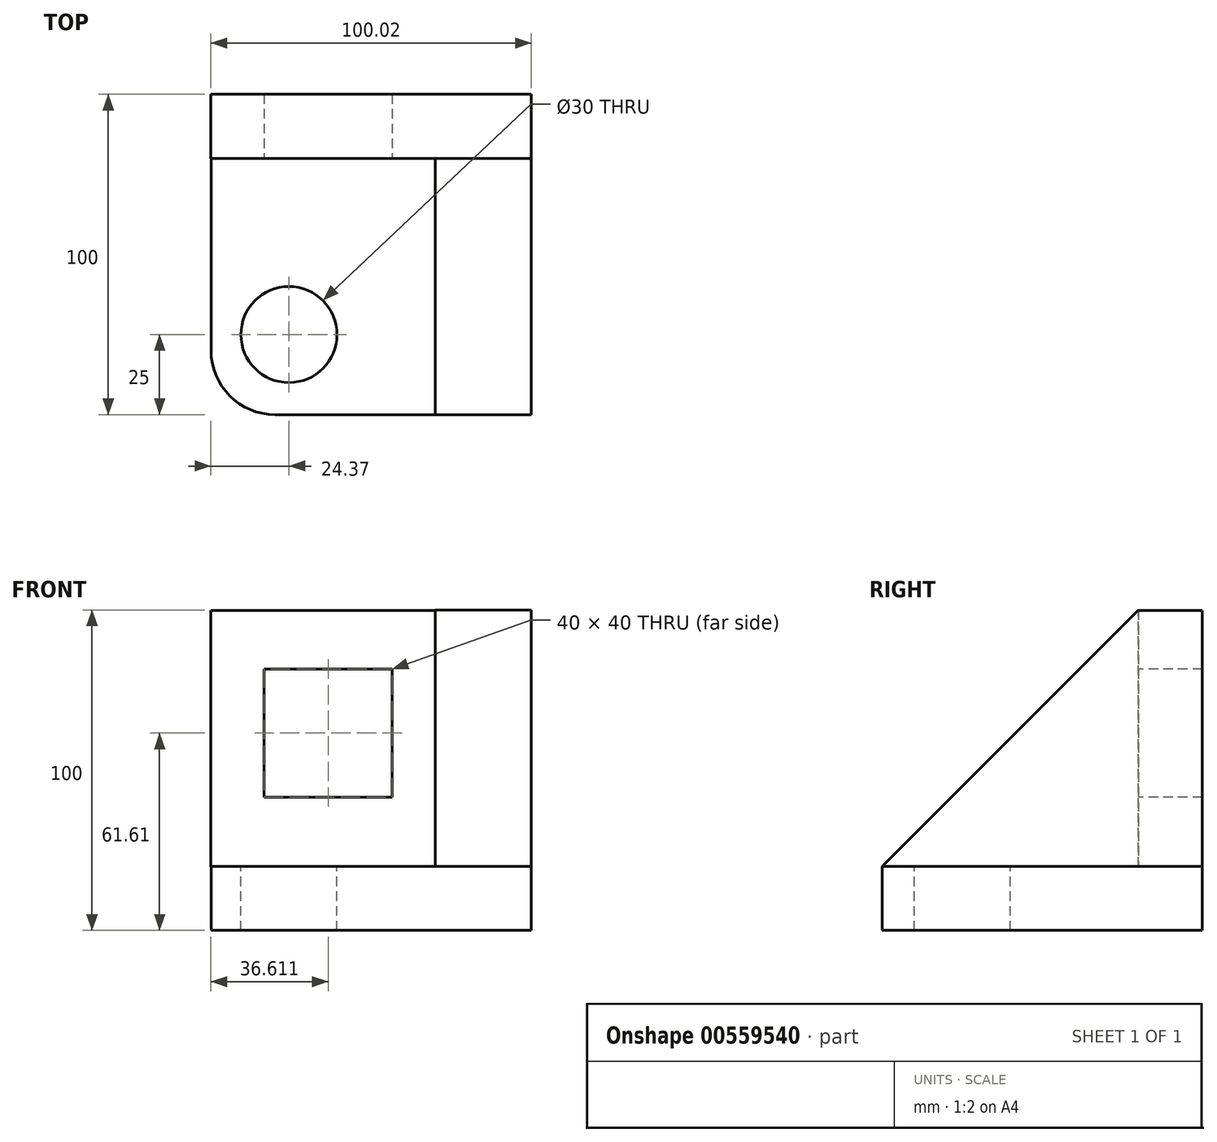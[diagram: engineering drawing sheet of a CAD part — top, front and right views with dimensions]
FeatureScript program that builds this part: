
annotation { "Feature Type Name" : "Feature", "Feature Type Description" : "" }
export const myFeature = defineFeature(function(context is Context, id is Id, definition is map)
    precondition{}
    {
        {
            var Q0;
            Q0=qCreatedBy(makeId("Top.planeOp"),FACE);
            var sketch = newSketch(context, id + "F0", { "sketchPlane" : qUnion([Q0])});
            skPoint(sketch, "E0.middle", {"position": v(0, 0) * mm});
            skLineSegment(sketch, "E1.bottom", {"start": v(-49.83, 0) * mm, "end": v(50.17, 0) * mm});
            skLineSegment(sketch, "E1.top", {"start": v(-49.83, -100) * mm, "end": v(50.17, -100) * mm});
            skLineSegment(sketch, "E1.left", {"start": v(-49.83, 0) * mm, "end": v(-49.83, -100) * mm});
            skLineSegment(sketch, "E1.right", {"start": v(50.17, 0) * mm, "end": v(50.17, -100) * mm});
            skSolve(sketch);
        }
        {
            var Q0;
            Q0 = qSketchRegion(id + "F0", true);
            extrude(context, id + "F1", {"entities" : qUnion([Q0]), "depth" : 20 * mm, "offsetDistance" : 25 * mm});
        }
        {
            var Q0;
            Q0=qCreatedBy(makeId("Front.planeOp"),FACE);
            var sketch = newSketch(context, id + "F2", { "sketchPlane" : qUnion([Q0])});
            skLineSegment(sketch, "E2.bottom", {"start": v(-49.85, 19.88) * mm, "end": v(50.15, 19.88) * mm});
            skLineSegment(sketch, "E2.top", {"start": v(-49.85, 99.88) * mm, "end": v(50.15, 99.88) * mm});
            skLineSegment(sketch, "E2.left", {"start": v(-49.85, 19.88) * mm, "end": v(-49.85, 99.88) * mm});
            skLineSegment(sketch, "E2.right", {"start": v(50.15, 19.88) * mm, "end": v(50.15, 99.88) * mm});
            skSolve(sketch);
        }
        {
            var Q0;
            Q0 = qSketchRegion(id + "F2", true);
            extrude(context, id + "F3", {"entities" : qUnion([Q0]), "operationType" : NewBodyOperationType.ADD, "depth" : 20 * mm, "offsetDistance" : 25 * mm});
        }
        {
            var Q0;
            Q0=makeQuery(id+"F1.opExtrude","CAP_FACE",FACE,{"disambiguationData":[OSD([sQuery(id+"F0.wireOp",EDGE,"E1.bottom"),sQuery(id+"F0.wireOp",EDGE,"E1.top"),sQuery(id+"F0.wireOp",EDGE,"E1.left"),sQuery(id+"F0.wireOp",EDGE,"E1.right")])],"isStart":false});
            var sketch = newSketch(context, id + "F4", { "sketchPlane" : qUnion([Q0])});
            skLineSegment(sketch, "E3.bottom", {"start": v(50.15, -20) * mm, "end": v(20.15, -20) * mm});
            skLineSegment(sketch, "E3.top", {"start": v(50.15, -100) * mm, "end": v(20.15, -100) * mm});
            skLineSegment(sketch, "E3.left", {"start": v(50.15, -20) * mm, "end": v(50.15, -100) * mm});
            skLineSegment(sketch, "E3.right", {"start": v(20.15, -20) * mm, "end": v(20.15, -100) * mm});
            skSolve(sketch);
        }
        {
            var Q0;
            Q0 = qSketchRegion(id + "F4", true);
            extrude(context, id + "F5", {"entities" : qUnion([Q0]), "operationType" : NewBodyOperationType.ADD, "depth" : 80 * mm, "offsetDistance" : 25 * mm});
        }
        {
            var Q0;
            Q0=makeQuery(id+"F1.opExtrude","SWEPT_EDGE",EDGE,{"disambiguationData":[OSD([sQuery(id+"F0.wireOp",EDGE,"E1.top"),sQuery(id+"F0.wireOp",EDGE,"E1.left")])]});
            fillet(context, id + "F6", {"entities" : qUnion([Q0]), "radius" : 20 * mm, "tangentPropagation" : true, "allowEdgeOverflow" : false});
        }
        {
            var Q0;
            {var subQ0=sQuery(id+"F0.wireOp",EDGE,"E1.top");var subQ1=sQuery(id+"F0.wireOp",EDGE,"E1.left");Q0=makeQuery(id+"F5.boolean.opBoolean","SPLIT",FACE,{"disambiguationData":[TD([makeQuery(id+"F1.opExtrude","SWEPT_FACE",FACE,{"disambiguationData":[OSD([subQ1])]})])],"derivedFrom":makeQuery(id+"F1.opExtrude","CAP_FACE",FACE,{"disambiguationData":[OSD([sQuery(id+"F0.wireOp",EDGE,"E1.bottom"),subQ0,subQ1,sQuery(id+"F0.wireOp",EDGE,"E1.right")])],"isStart":false})});}
            var sketch = newSketch(context, id + "F7", { "sketchPlane" : qUnion([Q0])});
            skCircle(sketch, "E4", {"center": v(-25.48, -75) * mm, "radius": 15 * mm});
            skSolve(sketch);
        }
        {
            var Q0;
            Q0 = qSketchRegion(id + "F7", true);
            extrude(context, id + "F8", {"entities" : qUnion([Q0]), "operationType" : NewBodyOperationType.REMOVE, "oppositeDirection" : true, "depth" : 20 * mm, "offsetDistance" : 25 * mm});
        }
        {
            var Q0;
            Q0=makeQuery(id+"F3.opExtrude","CAP_FACE",FACE,{"disambiguationData":[OSD([sQuery(id+"F2.wireOp",EDGE,"E2.bottom"),sQuery(id+"F2.wireOp",EDGE,"E2.top"),sQuery(id+"F2.wireOp",EDGE,"E2.left"),sQuery(id+"F2.wireOp",EDGE,"E2.right")])],"isStart":false});
            var sketch = newSketch(context, id + "F9", { "sketchPlane" : qUnion([Q0])});
            skLineSegment(sketch, "E5.bottom", {"start": v(6.76, 81.6) * mm, "end": v(-33.24, 81.6) * mm});
            skLineSegment(sketch, "E5.top", {"start": v(6.76, 41.6) * mm, "end": v(-33.24, 41.6) * mm});
            skLineSegment(sketch, "E5.left", {"start": v(6.76, 81.6) * mm, "end": v(6.76, 41.6) * mm});
            skLineSegment(sketch, "E5.right", {"start": v(-33.24, 81.6) * mm, "end": v(-33.24, 41.6) * mm});
            skSolve(sketch);
        }
        {
            var Q0;
            Q0 = qSketchRegion(id + "F9", true);
            extrude(context, id + "F10", {"entities" : qUnion([Q0]), "operationType" : NewBodyOperationType.REMOVE, "oppositeDirection" : true, "depth" : 20 * mm, "offsetDistance" : 25 * mm});
        }
        {
            var Q0;
            Q0=makeQuery(id+"F5.opExtrude","CAP_EDGE",EDGE,{"disambiguationData":[OSD([sQuery(id+"F4.wireOp",EDGE,"E3.top")])],"isStart":false});
            chamfer(context, id + "F11", {"entities" : qUnion([Q0]), "width" : 80 * mm, "tangentPropagation" : true});
        }
    });
